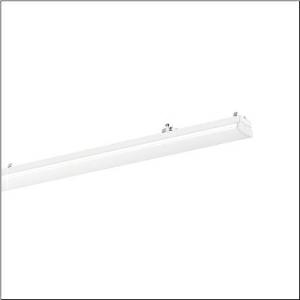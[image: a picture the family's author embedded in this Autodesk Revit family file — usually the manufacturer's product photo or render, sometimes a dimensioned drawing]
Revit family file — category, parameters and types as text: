
# Revit family: licross_11_recessed_opal_mo_51tl1dmn46xg
name_source: partatom
category: Lighting Fixtures
units: mm (PartAtom-declared; Revit-internal decimal feet)

## family parameters
Cut with Voids When Loaded = No
Host = Face
Light Source = No
Part Type = Normal
Room Calculation Point = No
Round Connector Dimension = Use Diameter
Shared = No

## types (1)
- --- (1 x LED, 6320 lm, 34.3 W, 4000K)
    Apparent Load = 34 VA
    CIE Flux Codes = 44 73 91 87 100
    Color Rendering = 80
    Color Temperature = 4000K
    Default Elevation = 1800 mm
    Description = Licross 11 recessed opal MO, luminaire insert, of sheet steel, coil coated, white, length: 1.500mm, width: 76mm, height: 87mm, LED rated luminous flux: 6.320lm, light colour: 840, SDCM (Standard Deviation of Colour Matching)MacAdam ≤ 2 SDCM (initial), control gear: ON/OFF Multilumen, with plug, 3-pole, with phase selection, mains connection: 220..240V, AC, 50/60Hz, rated input power: 34W, internal wiring halogen-free, primary optical cover: cover, of PMMA, light emission: direct with ceiling illumination distribution, primary light characteristic: symmetric, protection rating (complete): IP40, insulation class (complete): insulation class I (protective earthing), certification: CE, ENEC, VDE, UKCA, protection symbol: D if used in an environment without relevant dust loads with corresponding accessories, impact resistance: IK06, permissible ambient temperature for indoor applications: -35..+50°C, corresponds to IFS (International Featured Standards) requirements for safety and quality in the food industry, reducing of maximum allowable ambient temperature of 5°C with ceiling mounting, The light source and the operating device comply with the requirements of the Ecodesign Regulation (EU) 2019/2020 and are replaceable in accordance with this regulation, packaging unit: 1 piece
    Height = 83 mm
    Lamp = 1 x LED
    Lamp Light Flux = 6320 lm
    Lamp Power = 34.3 W
    Lamp count = 1
    Length = 1500 mm
    Luminous efficacy = 184 lm/W
    Manufacturer = Siteco
    ModVariant = No
    Model = 51TL1DMN46XG
    Mounting Place = Ceiling
    Mounting Type = Pendant
    Number of Poles = 1
    OnlyDefault = Yes
    Power Factor = 1
    Product Name = Licross 11 recessed opal MO
    Product group = luminaire insert | ceiling pendant
    ProductGroupID = 901
    Protection Class = Protection class I
    Protection Degree = IP 40
    RLX_Detail_Level = 1
    RLX_Emergency_Light_Flux = 0 lm
    RLX_Emergency_Type = 0
    RLX_Emergency_Type_DB = No
    RlxData = <blob elided: 24973 chars, md5=7bb2bd13>
    Socket = socket
    Standby Power = 0 W
    System Light Flux = 6320 lm
    System Power = 34 W
    Type Comments = factory setting: luminous flux: 100 % | (A | C | E) | 79 mA
    Type Image = l_1313666.jpg
    URL = http://relux.com
    VarID = @adj_070751
    Voltage = 0 V
    Weight = 0.00 kg
    Width = 76 mm

## geometry (parser evidence)
native form markers: Blend x4, Sweep x12
no freeform markers — native parametric forms only
